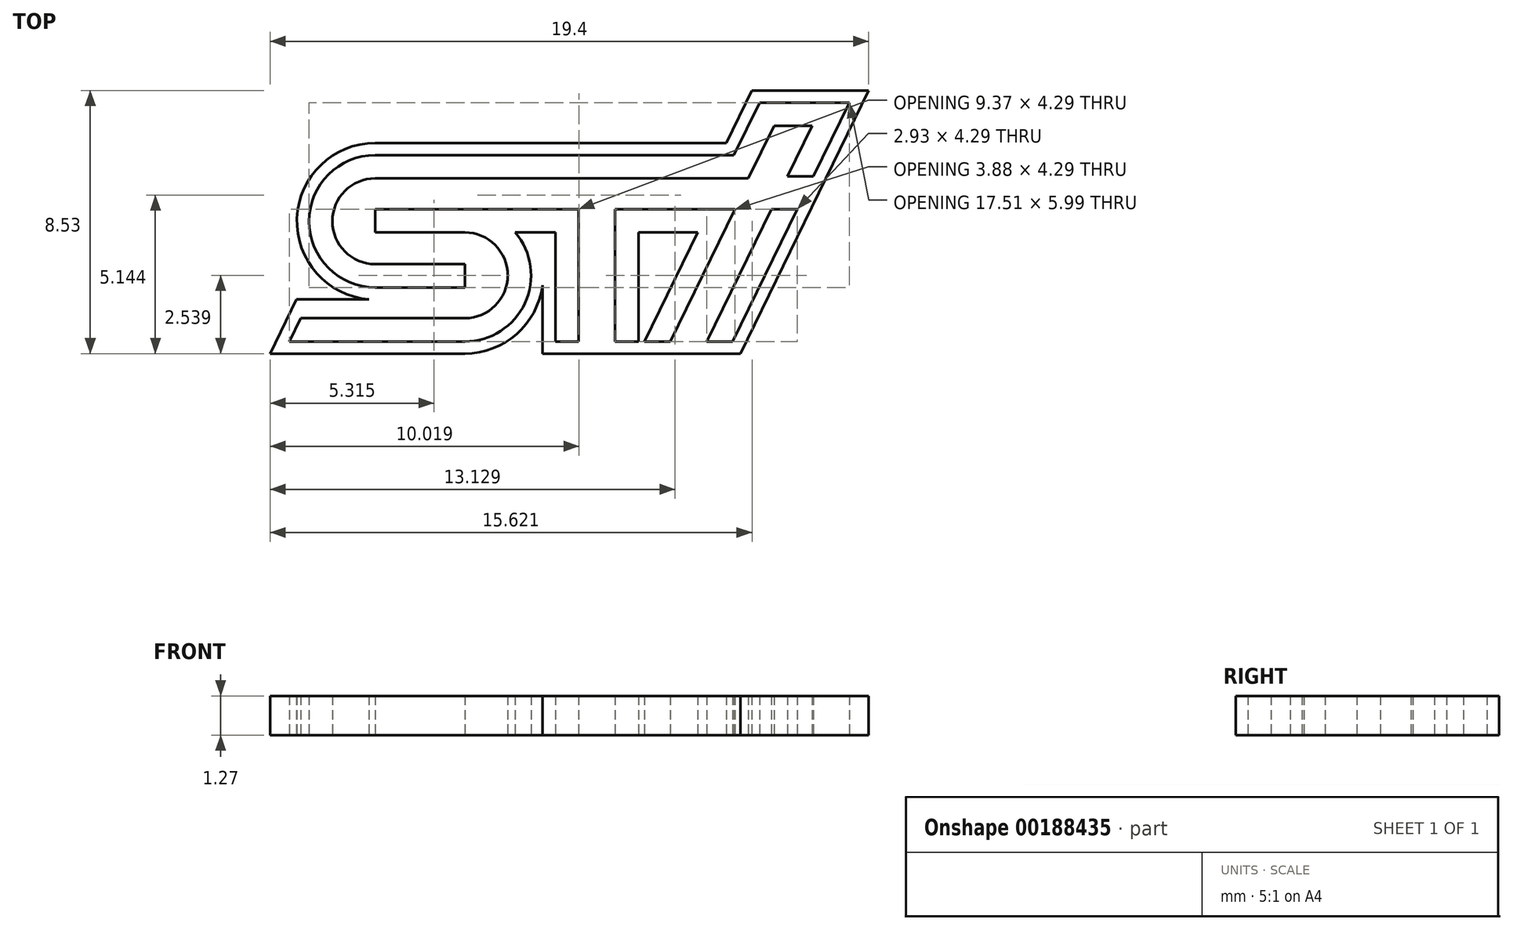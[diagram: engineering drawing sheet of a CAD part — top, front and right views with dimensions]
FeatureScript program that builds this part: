
annotation { "Feature Type Name" : "Feature", "Feature Type Description" : "" }
export const myFeature = defineFeature(function(context is Context, id is Id, definition is map)
    precondition{}
    {
        {
            var Q0;
            Q0=qCreatedBy(makeId("Top.planeOp"),FACE);
            var sketch = newSketch(context, id + "F0", { "sketchPlane" : qUnion([Q0])});
            skLineSegment(sketch, "E0", {"start": v(-144.68, -38.28) * mm, "end": v(-138.37, -38.28) * mm});
            skLineSegment(sketch, "E1", {"start": v(-144.68, -38.28) * mm, "end": v(-143.82, -36.52) * mm});
            skLineSegment(sketch, "E2", {"start": v(-143.82, -36.52) * mm, "end": v(-141.47, -36.52) * mm});
            skLineSegment(sketch, "E3", {"start": v(-135.85, -36.07) * mm, "end": v(-135.85, -38.28) * mm});
            skLineSegment(sketch, "E4", {"start": v(-135.85, -38.28) * mm, "end": v(-129.44, -38.28) * mm});
            skLineSegment(sketch, "E5", {"start": v(-129.44, -38.28) * mm, "end": v(-125.28, -29.75) * mm});
            skLineSegment(sketch, "E6", {"start": v(-125.28, -29.75) * mm, "end": v(-129.06, -29.75) * mm});
            skLineSegment(sketch, "E7", {"start": v(-129.06, -29.75) * mm, "end": v(-129.9, -31.45) * mm});
            skLineSegment(sketch, "E8", {"start": v(-129.9, -31.45) * mm, "end": v(-141.27, -31.45) * mm});
            skArc(sketch, "E9", {"start": v(-141.27, -31.45) * mm, "mid": v(-143.8, -33.89) * mm, "end": v(-141.47, -36.52) * mm});
            skArc(sketch, "E10", {"start": v(-138.37, -38.28) * mm, "mid": v(-136.7, -37.65) * mm, "end": v(-135.85, -36.07) * mm});
            skLineSegment(sketch, "E11", {"start": v(-138.37, -36.13) * mm, "end": v(-138.37, -35.38) * mm});
            skLineSegment(sketch, "E12", {"start": v(-138.37, -35.38) * mm, "end": v(-141.27, -35.38) * mm});
            skLineSegment(sketch, "E13", {"start": v(-138.37, -36.13) * mm, "end": v(-141.27, -36.13) * mm});
            skLineSegment(sketch, "E14", {"start": v(-141.27, -32.6) * mm, "end": v(-129.18, -32.6) * mm});
            skLineSegment(sketch, "E15", {"start": v(-129.18, -32.6) * mm, "end": v(-128.35, -30.9) * mm});
            skLineSegment(sketch, "E16", {"start": v(-128.35, -30.9) * mm, "end": v(-127.12, -30.9) * mm});
            skLineSegment(sketch, "E17", {"start": v(-127.12, -30.9) * mm, "end": v(-127.92, -32.53) * mm});
            skLineSegment(sketch, "E18", {"start": v(-127.92, -32.53) * mm, "end": v(-127.07, -32.53) * mm});
            skLineSegment(sketch, "E19", {"start": v(-127.07, -32.53) * mm, "end": v(-125.9, -30.14) * mm});
            skLineSegment(sketch, "E20", {"start": v(-125.9, -30.14) * mm, "end": v(-128.82, -30.14) * mm});
            skLineSegment(sketch, "E21", {"start": v(-128.82, -30.14) * mm, "end": v(-129.65, -31.84) * mm});
            skLineSegment(sketch, "E22", {"start": v(-129.65, -31.84) * mm, "end": v(-141.27, -31.84) * mm});
            skArc(sketch, "E23", {"start": v(-141.27, -31.84) * mm, "mid": v(-143.42, -33.99) * mm, "end": v(-141.27, -36.13) * mm});
            skArc(sketch, "E24", {"start": v(-141.27, -32.6) * mm, "mid": v(-142.66, -33.99) * mm, "end": v(-141.27, -35.38) * mm});
            skLineSegment(sketch, "E25", {"start": v(-144.05, -37.89) * mm, "end": v(-138.37, -37.89) * mm});
            skLineSegment(sketch, "E26", {"start": v(-144.05, -37.89) * mm, "end": v(-143.68, -37.13) * mm});
            skLineSegment(sketch, "E27", {"start": v(-143.68, -37.13) * mm, "end": v(-138.37, -37.13) * mm});
            skLineSegment(sketch, "E28", {"start": v(-138.37, -34.35) * mm, "end": v(-141.27, -34.35) * mm});
            skLineSegment(sketch, "E29", {"start": v(-141.27, -34.35) * mm, "end": v(-141.27, -33.6) * mm});
            skLineSegment(sketch, "E30", {"start": v(-141.27, -33.6) * mm, "end": v(-134.68, -33.6) * mm});
            skLineSegment(sketch, "E31", {"start": v(-134.68, -33.6) * mm, "end": v(-134.68, -37.89) * mm});
            skLineSegment(sketch, "E32", {"start": v(-134.68, -37.89) * mm, "end": v(-135.43, -37.89) * mm});
            skLineSegment(sketch, "E33", {"start": v(-135.43, -37.89) * mm, "end": v(-135.43, -34.35) * mm});
            skLineSegment(sketch, "E34", {"start": v(-135.43, -34.35) * mm, "end": v(-136.73, -34.35) * mm});
            skArc(sketch, "E35", {"start": v(-138.37, -37.13) * mm, "mid": v(-136.98, -35.74) * mm, "end": v(-138.37, -34.35) * mm});
            skArc(sketch, "E36", {"start": v(-138.37, -37.89) * mm, "mid": v(-136.42, -36.64) * mm, "end": v(-136.73, -34.35) * mm});
            skLineSegment(sketch, "E37", {"start": v(-133.5, -37.89) * mm, "end": v(-132.74, -37.89) * mm});
            skLineSegment(sketch, "E38", {"start": v(-132.74, -37.89) * mm, "end": v(-132.74, -34.35) * mm});
            skLineSegment(sketch, "E39", {"start": v(-132.74, -34.35) * mm, "end": v(-130.82, -34.35) * mm});
            skLineSegment(sketch, "E40", {"start": v(-130.82, -34.35) * mm, "end": v(-132.54, -37.89) * mm});
            skLineSegment(sketch, "E41", {"start": v(-132.54, -37.89) * mm, "end": v(-131.7, -37.89) * mm});
            skLineSegment(sketch, "E42", {"start": v(-131.7, -37.89) * mm, "end": v(-129.6, -33.6) * mm});
            skLineSegment(sketch, "E43", {"start": v(-129.6, -33.6) * mm, "end": v(-133.5, -33.6) * mm});
            skLineSegment(sketch, "E44", {"start": v(-133.5, -33.6) * mm, "end": v(-133.5, -37.89) * mm});
            skLineSegment(sketch, "E45", {"start": v(-130.53, -37.89) * mm, "end": v(-129.69, -37.89) * mm});
            skLineSegment(sketch, "E46", {"start": v(-129.69, -37.89) * mm, "end": v(-127.6, -33.6) * mm});
            skLineSegment(sketch, "E47", {"start": v(-127.6, -33.6) * mm, "end": v(-128.43, -33.6) * mm});
            skLineSegment(sketch, "E48", {"start": v(-130.53, -37.89) * mm, "end": v(-128.43, -33.6) * mm});
            skSolve(sketch);
        }
        {
            var Q0;
            Q0=makeQuery(id+"F0.imprint","IMPRINT",FACE,{"disambiguationData":[TD([[makeQuery(id+"F0.imprint","IMPRINT",EDGE,{"derivedFrom":sQuery(id+"F0.wireOp",EDGE,"E0")}),1.0]])]});
            extrude(context, id + "F1", {"entities" : qUnion([Q0]), "depth" : 1.27 * mm});
        }
    });
